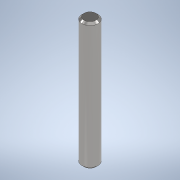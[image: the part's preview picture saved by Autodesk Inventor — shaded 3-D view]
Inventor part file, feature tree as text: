
AUTODESK INVENTOR PART (.ipt)
format: ipt  version: 2021 (Build 250183000, 183)  size: 96,256 bytes
history: native  units: mm
features: extrude x1, chamfer x1, sketch x1
ambient origin geometry x8: Origin, YZ Plane, XZ Plane, XY Plane, X Axis, Y Axis, Z Axis, Center Point
bodies: Solid1 (feature_tree)
feature tree (3):
  extrude  "Extrusion1"  Depth=63.0mm TaperAngle=0.0deg
  chamfer  "Chamfer1"  Distance=1.0mm Angle=45.0deg
  sketch  "Sketch1"  dims[d0=8.0mm d1=63.0mm d2=0.0mm d3=1.0mm d4=2.0mm d5=45.0deg]
